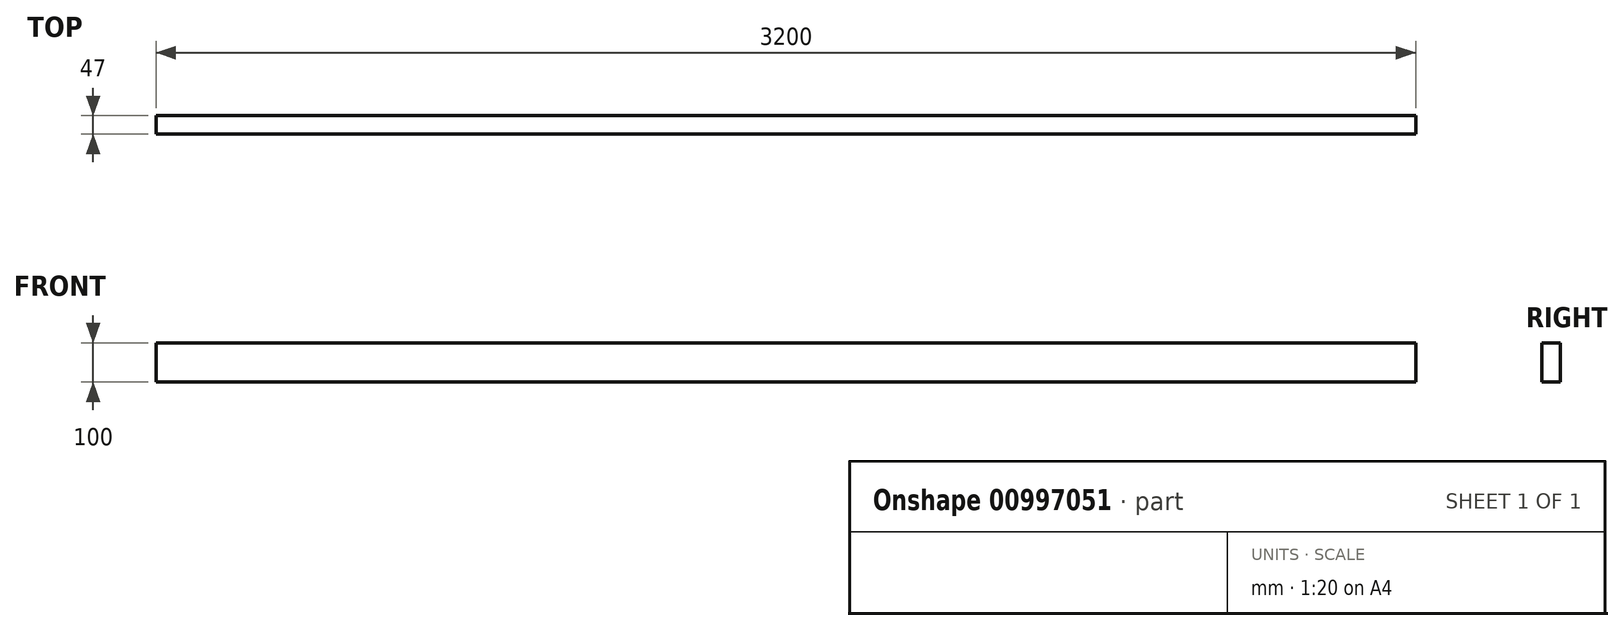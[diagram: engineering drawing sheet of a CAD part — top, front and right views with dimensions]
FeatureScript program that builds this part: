
annotation { "Feature Type Name" : "Feature", "Feature Type Description" : "" }
export const myFeature = defineFeature(function(context is Context, id is Id, definition is map)
    precondition{}
    {
        {
            var Q0;
            Q0=qCreatedBy(makeId("Right.planeOp"),FACE);
            var sketch = newSketch(context, id + "F0", { "sketchPlane" : qUnion([Q0])});
            skLineSegment(sketch, "E0.bottom", {"start": v(-33.62, 10.82) * mm, "end": v(13.38, 10.82) * mm});
            skLineSegment(sketch, "E0.top", {"start": v(-33.62, 110.82) * mm, "end": v(13.38, 110.82) * mm});
            skLineSegment(sketch, "E0.left", {"start": v(-33.62, 10.82) * mm, "end": v(-33.62, 110.82) * mm});
            skLineSegment(sketch, "E0.right", {"start": v(13.38, 10.82) * mm, "end": v(13.38, 110.82) * mm});
            skSolve(sketch);
        }
        {
            var Q0;
            Q0=makeQuery(id+"F0.imprint","IMPRINT",FACE,{"disambiguationData":[TD([[makeQuery(id+"F0.imprint","IMPRINT",EDGE,{"derivedFrom":sQuery(id+"F0.wireOp",EDGE,"E0.bottom")}),1.0]])]});
            extrude(context, id + "F1", {"entities" : qUnion([Q0]), "depth" : 3200 * mm, "offsetDistance" : 25 * mm});
        }
    });
